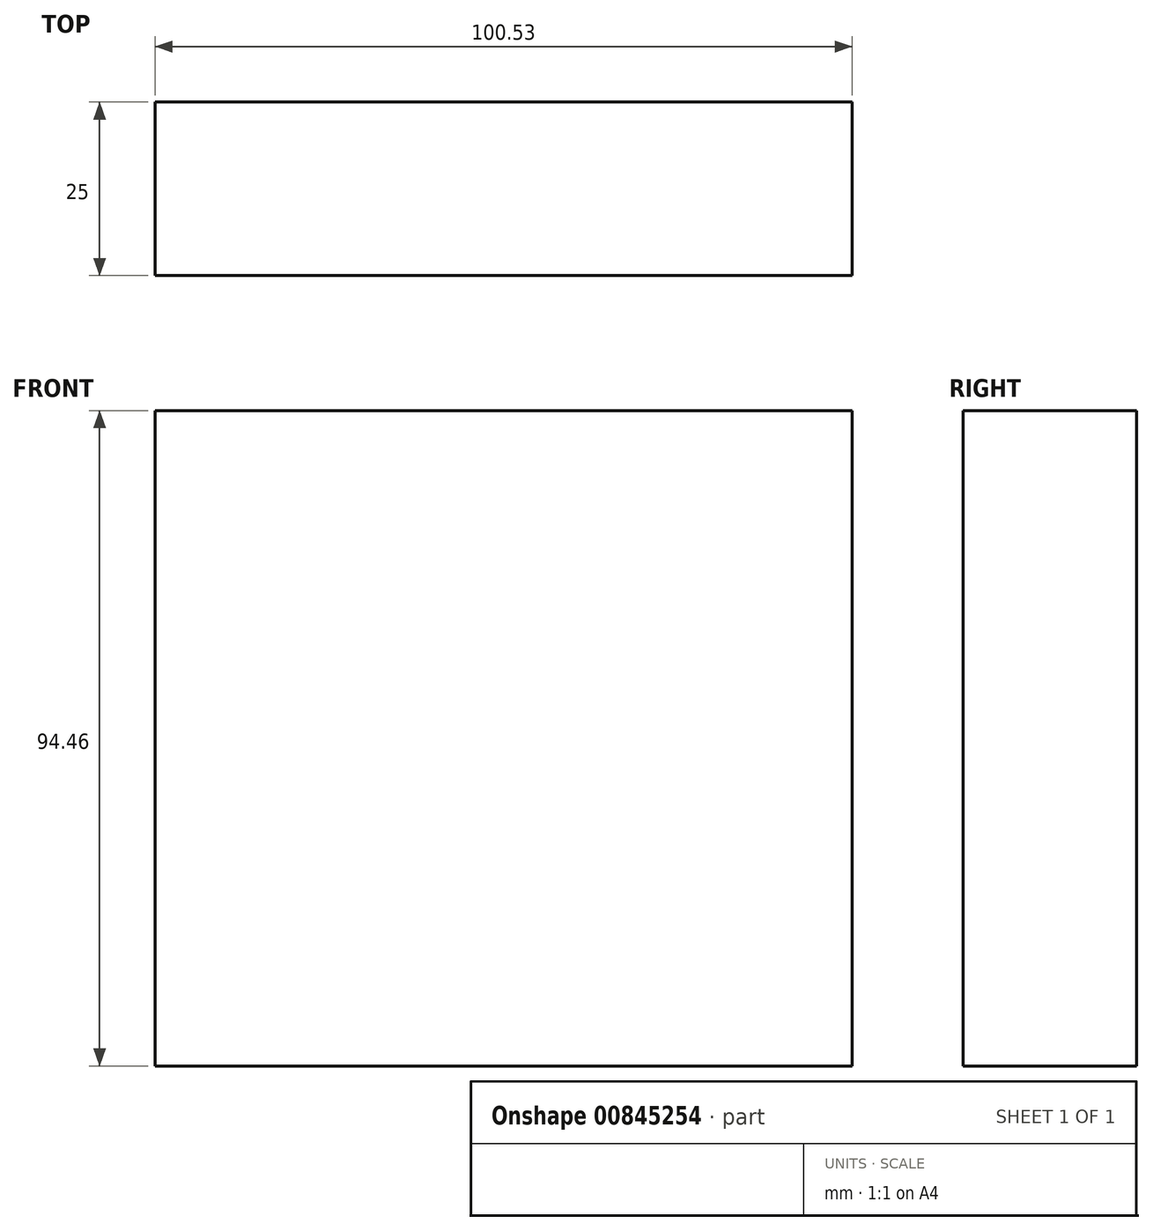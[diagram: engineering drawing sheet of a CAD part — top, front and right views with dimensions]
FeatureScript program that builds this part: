
annotation { "Feature Type Name" : "Feature", "Feature Type Description" : "" }
export const myFeature = defineFeature(function(context is Context, id is Id, definition is map)
    precondition{}
    {
        {
            var Q0;
            Q0=qCreatedBy(makeId("Front.planeOp"),FACE);
            var sketch = newSketch(context, id + "F0", { "sketchPlane" : qUnion([Q0])});
            skLineSegment(sketch, "E0.bottom", {"start": v(-250.13, -38.89) * mm, "end": v(-149.6, -38.89) * mm});
            skLineSegment(sketch, "E0.top", {"start": v(-250.13, 55.57) * mm, "end": v(-149.6, 55.57) * mm});
            skLineSegment(sketch, "E0.left", {"start": v(-250.13, -38.89) * mm, "end": v(-250.13, 55.57) * mm});
            skLineSegment(sketch, "E0.right", {"start": v(-149.6, -38.89) * mm, "end": v(-149.6, 55.57) * mm});
            skPoint(sketch, "E0.middle", {"position": v(-199.86, 8.34) * mm});
            skSolve(sketch);
        }
        {
            var Q0;
            Q0=makeQuery(id+"F0.imprint","IMPRINT",FACE,{"disambiguationData":[TD([[makeQuery(id+"F0.imprint","IMPRINT",EDGE,{"derivedFrom":sQuery(id+"F0.wireOp",EDGE,"E0.bottom")}),1.0]])]});
            extrude(context, id + "F1", {"entities" : qUnion([Q0]), "depth" : 25 * mm, "offsetDistance" : 25 * mm});
        }
    });
